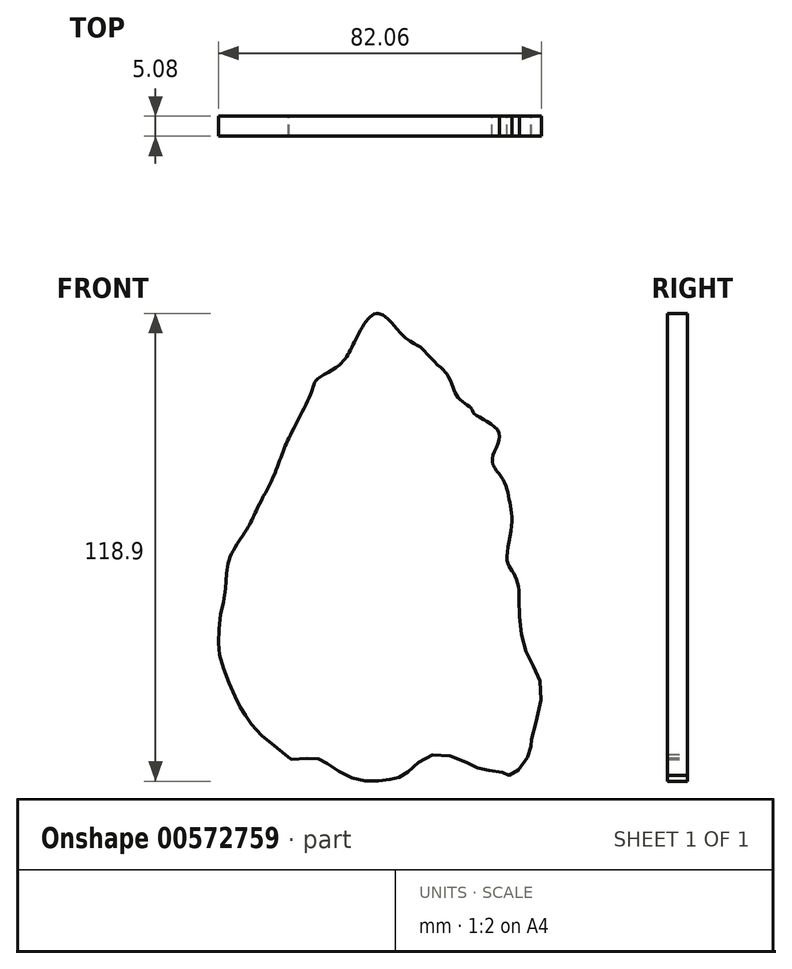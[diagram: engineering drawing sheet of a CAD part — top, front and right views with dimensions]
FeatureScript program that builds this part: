
annotation { "Feature Type Name" : "Feature", "Feature Type Description" : "" }
export const myFeature = defineFeature(function(context is Context, id is Id, definition is map)
    precondition{}
    {
        {
            var Q0;
            Q0=qCreatedBy(makeId("Front.planeOp"),FACE);
            var sketch = newSketch(context, id + "F0", { "sketchPlane" : qUnion([Q0])});
            skFitSpline(sketch, "E0", {"points": [v(0, 62.78) * mm, v(-5.55, 56.65) * mm, v(-9.93, 49.64) * mm, v(-15.77, 45.85) * mm, v(-16.64, 43.8) * mm, v(-18.4, 39.71) * mm, v(-21.9, 32.7) * mm, v(-24.24, 27.74) * mm, v(-26.28, 22.2) * mm, v(-30.66, 13.43) * mm, v(-33.29, 8.18) * mm, v(-37.96, 0) * mm, v(-38.84, -7.88) * mm, v(-40, -13.43) * mm, v(-40.59, -20.15) * mm, v(-40, -25.4) * mm, v(-37.38, -32.41) * mm, v(-35.04, -37.38) * mm, v(-33.29, -40) * mm, v(-29.5, -44.68) * mm, v(-22.78, -50.23) * mm, v(-22.78, -50.52) * mm, v(-16.94, -50.23) * mm, v(-14.3, -50.8) * mm, v(-9.34, -54.02) * mm, v(-3.21, -56.07) * mm, v(2.04, -55.77) * mm, v(4.96, -55.19) * mm, v(7.88, -53.44) * mm, v(14.02, -49.35) * mm, v(23.07, -51.69) * mm, v(26.86, -53.15) * mm, v(32.12, -54.02) * mm, v(33.29, -54.6) * mm, v(37.08, -51.4) * mm, v(38.84, -47.01) * mm, v(38.84, -45.85) * mm, v(41.47, -33.58) * mm, v(38.54, -25.4) * mm, v(35.92, -16.06) * mm, v(35.62, -7.3) * mm, v(34.16, -2.92) * mm, v(32.7, 0) * mm, v(33.87, 9.05) * mm, v(33.29, 15.18) * mm, v(31.54, 20.73) * mm, v(28.9, 25.7) * mm, v(30.66, 32.41) * mm, v(24.24, 37.38) * mm, v(23.65, 38.54) * mm, v(20.73, 40.88) * mm, v(18.69, 44.68) * mm, v(17.23, 47.6) * mm, v(15.77, 49.06) * mm, v(11.97, 52.85) * mm, v(10.51, 54.31) * mm, v(6.42, 56.94) * mm, v(0, 62.78) * mm]});
            skLineSegment(sketch, "E1", {"start": v(0, 62.78) * mm, "end": v(0, -56.03) * mm});
            skLineSegment(sketch, "E2", {"start": v(0, 21.9) * mm, "end": v(18.69, 44.68) * mm});
            skLineSegment(sketch, "E3", {"start": v(0, 15.77) * mm, "end": v(-21.9, 32.7) * mm});
            skLineSegment(sketch, "E4", {"start": v(0, 8.76) * mm, "end": v(30.66, 32.41) * mm});
            skLineSegment(sketch, "E5", {"start": v(0, -6.13) * mm, "end": v(-30.66, 13.43) * mm});
            skLineSegment(sketch, "E6", {"start": v(-0.87, -18.98) * mm, "end": v(33.7, 13) * mm});
            skLineSegment(sketch, "E7", {"start": v(0, -30.95) * mm, "end": v(-38.58, -3.32) * mm});
            skLineSegment(sketch, "E8", {"start": v(0, -39.71) * mm, "end": v(35.77, -9.9) * mm});
            skLineSegment(sketch, "E9", {"start": v(-9.93, 49.64) * mm, "end": v(0, 39.71) * mm});
            skSolve(sketch);
        }
        {
            var Q0;
            {var subQ3=sQuery(id+"F0.wireOp",EDGE,"E9");Q0=makeQuery(id+"F0.imprint","IMPRINT",FACE,{"disambiguationData":[TD([[makeQuery(id+"F0.imprint","IMPRINT",EDGE,{"derivedFrom":subQ3}),1.0]])]});}
            var Q1;
            {var subQ3=sQuery(id+"F0.wireOp",EDGE,"E2");Q1=makeQuery(id+"F0.imprint","IMPRINT",FACE,{"disambiguationData":[TD([[makeQuery(id+"F0.imprint","IMPRINT",EDGE,{"derivedFrom":subQ3}),1.0]])]});}
            var Q2;
            {var subQ0=sQuery(id+"F0.wireOp",EDGE,"E3");Q2=makeQuery(id+"F0.imprint","IMPRINT",FACE,{"disambiguationData":[TD([[makeQuery(id+"F0.imprint","IMPRINT",EDGE,{"derivedFrom":subQ0}),1.0]])]});}
            var Q3;
            {var subQ0=sQuery(id+"F0.wireOp",EDGE,"E2");Q3=makeQuery(id+"F0.imprint","IMPRINT",FACE,{"disambiguationData":[TD([[makeQuery(id+"F0.imprint","IMPRINT",EDGE,{"derivedFrom":subQ0}),-1.0]])]});}
            var Q4;
            {var subQ0=sQuery(id+"F0.wireOp",EDGE,"E4");Q4=makeQuery(id+"F0.imprint","IMPRINT",FACE,{"disambiguationData":[TD([[makeQuery(id+"F0.imprint","IMPRINT",EDGE,{"derivedFrom":subQ0}),-1.0]])]});}
            var Q5;
            {var subQ0=sQuery(id+"F0.wireOp",EDGE,"E5");Q5=makeQuery(id+"F0.imprint","IMPRINT",FACE,{"disambiguationData":[TD([[makeQuery(id+"F0.imprint","IMPRINT",EDGE,{"derivedFrom":subQ0}),1.0]])]});}
            var Q6;
            {var subQ3=sQuery(id+"F0.wireOp",EDGE,"E7");Q6=makeQuery(id+"F0.imprint","IMPRINT",FACE,{"disambiguationData":[TD([[makeQuery(id+"F0.imprint","IMPRINT",EDGE,{"derivedFrom":subQ3}),1.0]])]});}
            var Q7;
            {var subQ6=sQuery(id+"F0.wireOp",EDGE,"E8");Q7=makeQuery(id+"F0.imprint","IMPRINT",FACE,{"disambiguationData":[TD([[makeQuery(id+"F0.imprint","IMPRINT",EDGE,{"derivedFrom":subQ6}),1.0]])]});}
            var Q8;
            {var subQ3=sQuery(id+"F0.wireOp",EDGE,"E8");Q8=makeQuery(id+"F0.imprint","IMPRINT",FACE,{"disambiguationData":[TD([[makeQuery(id+"F0.imprint","IMPRINT",EDGE,{"derivedFrom":subQ3}),-1.0]])]});}
            var Q9;
            {var subQ0=sQuery(id+"F0.wireOp",EDGE,"E3");Q9=makeQuery(id+"F0.imprint","IMPRINT",FACE,{"disambiguationData":[TD([[makeQuery(id+"F0.imprint","IMPRINT",EDGE,{"derivedFrom":subQ0}),-1.0]])]});}
            extrude(context, id + "F1", {"entities" : qUnion([Q0, Q1, Q2, Q3, Q4, Q5, Q6, Q7, Q8, Q9]), "depth" : 5.08 * mm, "offsetDistance" : 25.4 * mm});
        }
    });
